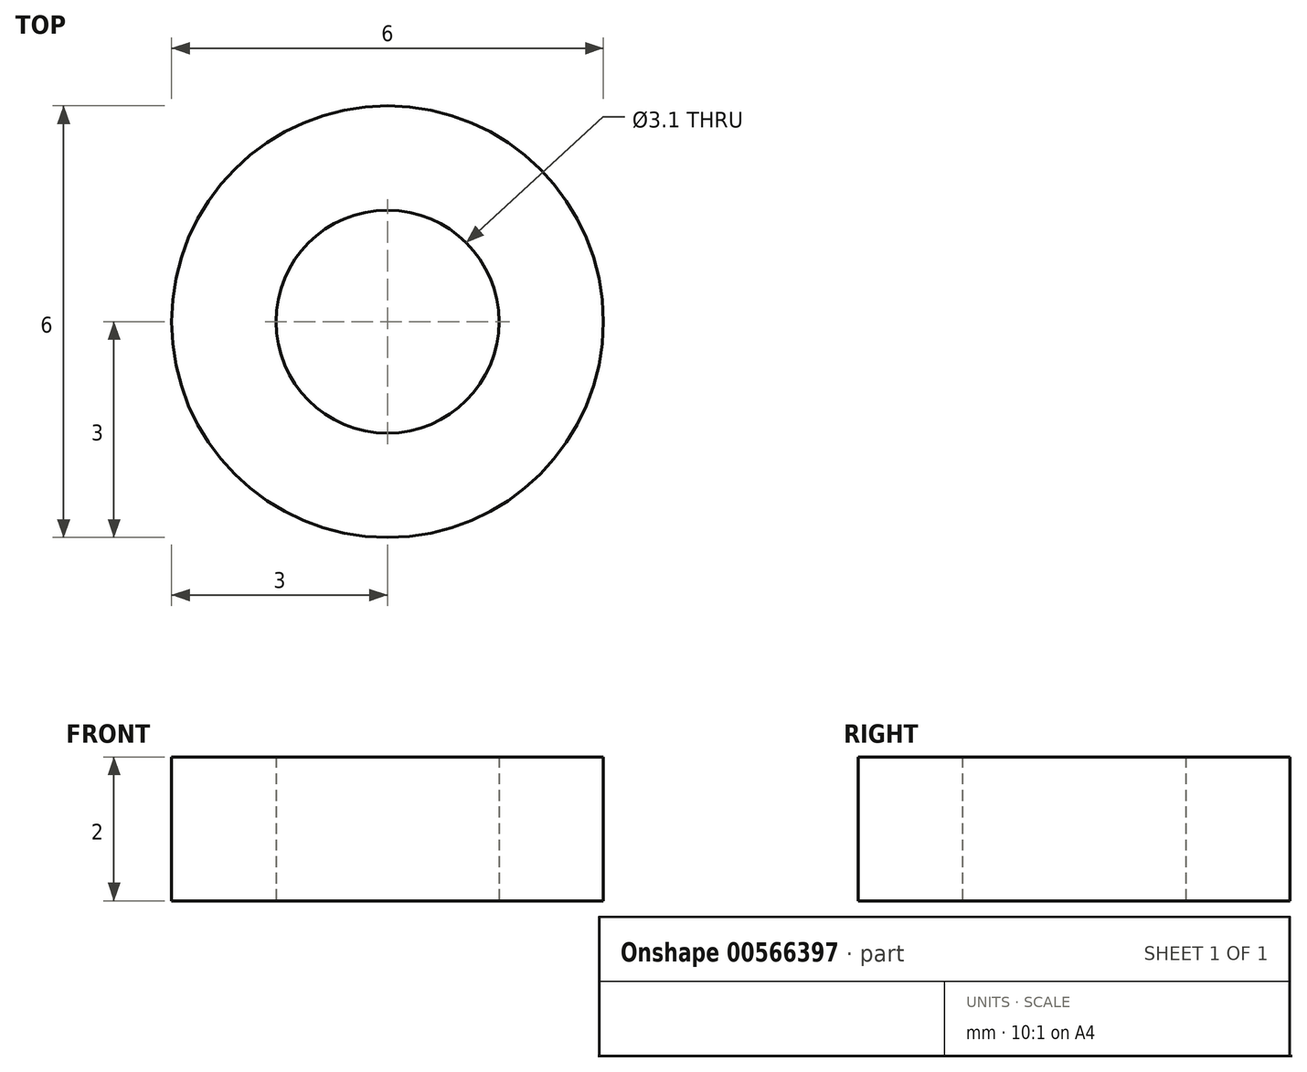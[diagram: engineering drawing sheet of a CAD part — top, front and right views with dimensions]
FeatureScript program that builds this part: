
annotation { "Feature Type Name" : "Feature", "Feature Type Description" : "" }
export const myFeature = defineFeature(function(context is Context, id is Id, definition is map)
    precondition{}
    {
        {
            var Q0;
            Q0=qCreatedBy(makeId("Top.planeOp"),FACE);
            var sketch = newSketch(context, id + "F0", { "sketchPlane" : qUnion([Q0])});
            skCircle(sketch, "E0", {"center": v(0, 0) * mm, "radius": 1.55 * mm});
            skCircle(sketch, "E1", {"center": v(0, 0) * mm, "radius": 3 * mm});
            skSolve(sketch);
        }
        {
            var Q0;
            Q0=qSketchRegion(id+"F0",true);
            extrude(context, id + "F1", {"entities" : qUnion([Q0]), "depth" : 2 * mm, "offsetDistance" : 25 * mm});
        }
    });
